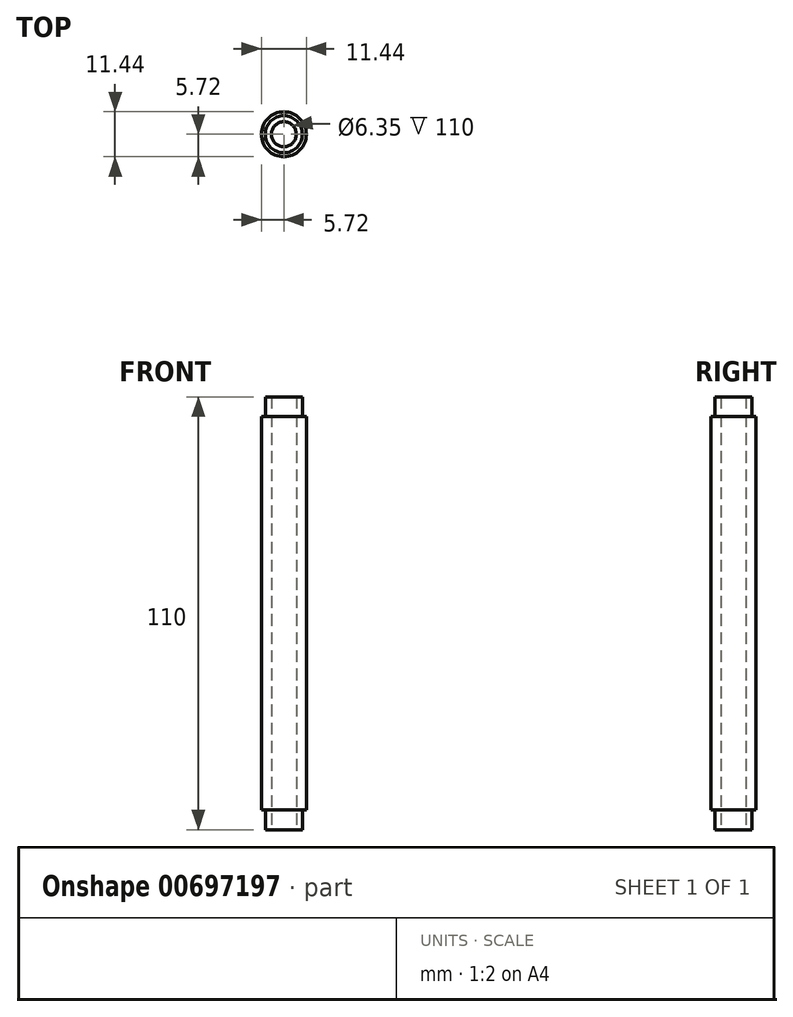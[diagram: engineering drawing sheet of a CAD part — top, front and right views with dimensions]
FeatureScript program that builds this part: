
annotation { "Feature Type Name" : "Feature", "Feature Type Description" : "" }
export const myFeature = defineFeature(function(context is Context, id is Id, definition is map)
    precondition{}
    {
        {
            var Q0;
            Q0=qCreatedBy(makeId("Top.planeOp"),FACE);
            var sketch = newSketch(context, id + "F0", { "sketchPlane" : qUnion([Q0])});
            skCircle(sketch, "E0", {"center": v(0, 0) * mm, "radius": 3.18 * mm});
            skCircle(sketch, "E1", {"center": v(0, 0) * mm, "radius": 5.71 * mm});
            skSolve(sketch);
        }
        {
            var Q0;
            Q0=makeQuery(id+"F0.imprint","IMPRINT",FACE,{"disambiguationData":[TD([[makeQuery(id+"F0.imprint","IMPRINT",EDGE,{"derivedFrom":sQuery(id+"F0.wireOp",EDGE,"E0")}),-1.0]])]});
            extrude(context, id + "F1", {"entities" : qUnion([Q0]), "depth" : 100 * mm, "offsetDistance" : 25 * mm});
        }
        {
            var Q0;
            Q0=makeQuery(id+"F1.opExtrude","CAP_FACE",FACE,{"disambiguationData":[OSD([sQuery(id+"F0.wireOp",EDGE,"E0"),sQuery(id+"F0.wireOp",EDGE,"E1")])],"isStart":false});
            var sketch = newSketch(context, id + "F2", { "sketchPlane" : qUnion([Q0])});
            skCircle(sketch, "E2", {"center": v(0, 0) * mm, "radius": 3.17 * mm});
            skCircle(sketch, "E3", {"center": v(0, 0) * mm, "radius": 4.7 * mm});
            skSolve(sketch);
        }
        {
            var Q0;
            Q0=makeQuery(id+"F2.imprint","IMPRINT",FACE,{"disambiguationData":[TD([[makeQuery(id+"F2.imprint","IMPRINT",EDGE,{"derivedFrom":sQuery(id+"F2.wireOp",EDGE,"E2")}),-1.0]])]});
            extrude(context, id + "F3", {"entities" : qUnion([Q0]), "operationType" : NewBodyOperationType.ADD, "depth" : 5 * mm, "offsetDistance" : 25 * mm});
        }
        {
            var Q0;
            Q0=qCreatedBy(makeId("Top.planeOp"),FACE);
            var sketch = newSketch(context, id + "F4", { "sketchPlane" : qUnion([Q0])});
            skCircle(sketch, "E4", {"center": v(0, 0) * mm, "radius": 3.17 * mm});
            skCircle(sketch, "E5", {"center": v(0, 0) * mm, "radius": 4.7 * mm});
            skSolve(sketch);
        }
        {
            var Q0;
            Q0=makeQuery(id+"F4.imprint","IMPRINT",FACE,{"disambiguationData":[TD([[makeQuery(id+"F4.imprint","IMPRINT",EDGE,{"derivedFrom":sQuery(id+"F4.wireOp",EDGE,"E4")}),-1.0]])]});
            extrude(context, id + "F5", {"entities" : qUnion([Q0]), "operationType" : NewBodyOperationType.ADD, "oppositeDirection" : true, "depth" : 5 * mm, "offsetDistance" : 25 * mm});
        }
    });
